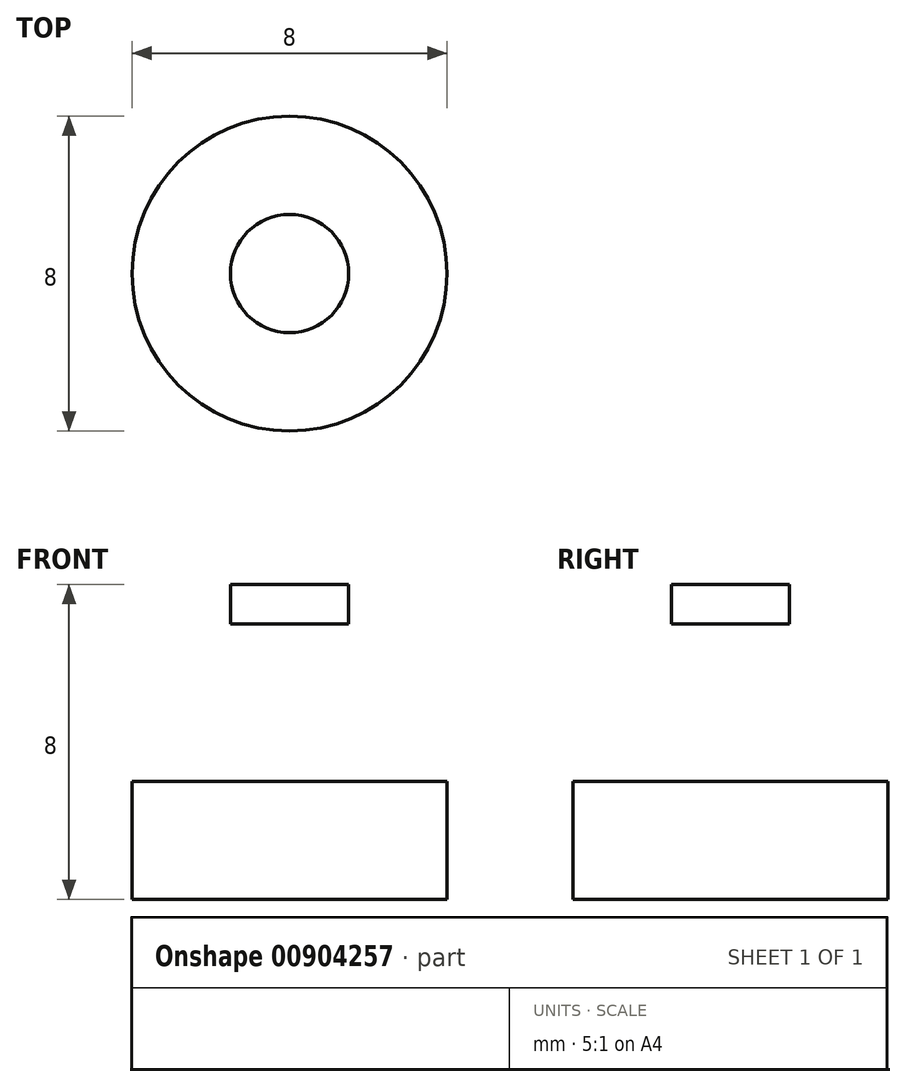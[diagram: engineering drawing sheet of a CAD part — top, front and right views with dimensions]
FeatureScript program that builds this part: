
annotation { "Feature Type Name" : "Feature", "Feature Type Description" : "" }
export const myFeature = defineFeature(function(context is Context, id is Id, definition is map)
    precondition{}
    {
        {
            var Q0;
            Q0=qCreatedBy(makeId("Front.planeOp"),FACE);
            var sketch = newSketch(context, id + "F0", { "sketchPlane" : qUnion([Q0])});
            skLineSegment(sketch, "E0.bottom", {"start": v(0, 0) * mm, "end": v(-4, 0) * mm});
            skLineSegment(sketch, "E0.top", {"start": v(0, 3) * mm, "end": v(-4, 3) * mm});
            skLineSegment(sketch, "E0.left", {"start": v(0, 0) * mm, "end": v(0, 3) * mm});
            skLineSegment(sketch, "E0.right", {"start": v(-4, 0) * mm, "end": v(-4, 3) * mm});
            skLineSegment(sketch, "E1.bottom", {"start": v(0, 3) * mm, "end": v(-1, 3) * mm});
            skLineSegment(sketch, "E1.top", {"start": v(0, 7) * mm, "end": v(-1, 7) * mm});
            skLineSegment(sketch, "E1.left", {"start": v(0, 3) * mm, "end": v(0, 7) * mm});
            skLineSegment(sketch, "E1.right", {"start": v(-1, 3) * mm, "end": v(-1, 7) * mm});
            skLineSegment(sketch, "E2.bottom", {"start": v(0, 7) * mm, "end": v(-1.5, 7) * mm});
            skLineSegment(sketch, "E2.top", {"start": v(0, 8) * mm, "end": v(-1.5, 8) * mm});
            skLineSegment(sketch, "E2.left", {"start": v(0, 7) * mm, "end": v(0, 8) * mm});
            skLineSegment(sketch, "E2.right", {"start": v(-1.5, 7) * mm, "end": v(-1.5, 8) * mm});
            skSolve(sketch);
        }
        {
            var Q0;
            Q0=makeQuery(id+"F0.imprint","IMPRINT",FACE,{"disambiguationData":[TD([[makeQuery(id+"F0.imprint","IMPRINT",EDGE,{"derivedFrom":sQuery(id+"F0.wireOp",EDGE,"E0.bottom")}),-1.0]])]});
            var Q1;
            Q1=makeQuery(id+"F0.imprint","IMPRINT",FACE,{"disambiguationData":[TD([[makeQuery(id+"F0.imprint","IMPRINT",EDGE,{"derivedFrom":sQuery(id+"F0.wireOp",EDGE,"E1.bottom")}),-1.0]])]});
            var Q2;
            Q2=makeQuery(id+"F0.imprint","IMPRINT",FACE,{"disambiguationData":[TD([[makeQuery(id+"F0.imprint","IMPRINT",EDGE,{"derivedFrom":sQuery(id+"F0.wireOp",EDGE,"E2.top")}),1.0]])]});
            var Q3;
            Q3=sQuery(id+"F0.wireOp",EDGE,"E0.left");
            revolve(context, id + "F1", {"surfaceOperationType" : NewSurfaceOperationType.NEW, "entities" : qUnion([Q0, Q1, Q2]), "axis" : qUnion([Q3]), "revolveType" : RevolveType.FULL});
        }
    });
